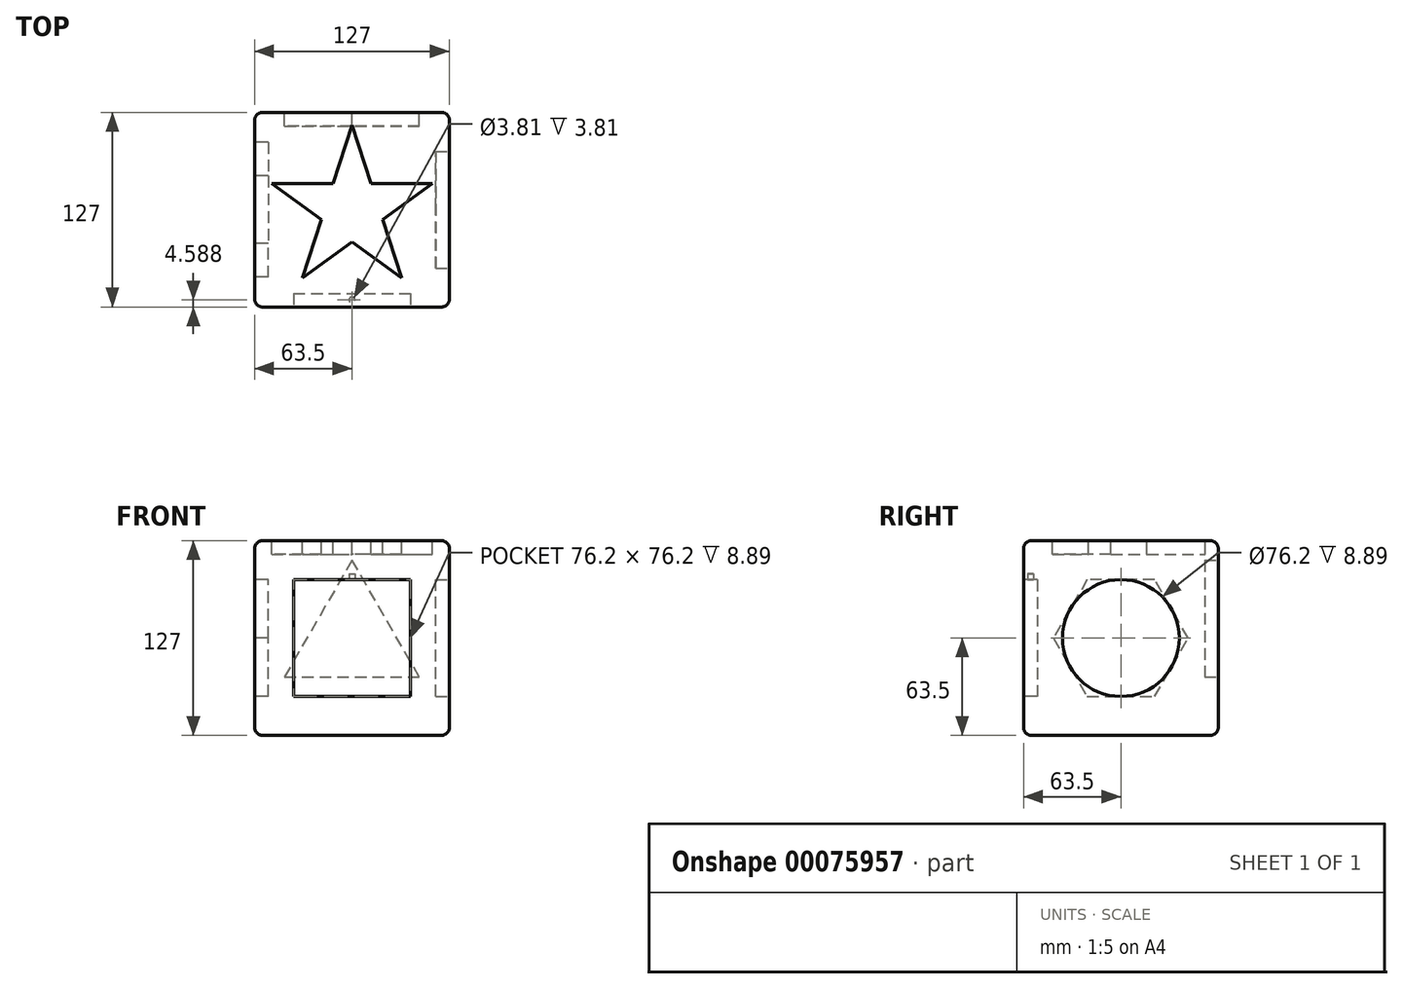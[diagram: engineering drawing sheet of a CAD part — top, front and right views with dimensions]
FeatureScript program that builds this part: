
annotation { "Feature Type Name" : "Feature", "Feature Type Description" : "" }
export const myFeature = defineFeature(function(context is Context, id is Id, definition is map)
    precondition{}
    {
        {
            var Q0;
            Q0=qCreatedBy(makeId("Top.planeOp"),FACE);
            var sketch = newSketch(context, id + "F0", { "sketchPlane" : qUnion([Q0])});
            skLineSegment(sketch, "E0.bottom", {"start": v(-63.5, 63.5) * mm, "end": v(63.5, 63.5) * mm});
            skLineSegment(sketch, "E0.top", {"start": v(-63.5, -63.5) * mm, "end": v(63.5, -63.5) * mm});
            skLineSegment(sketch, "E0.left", {"start": v(-63.5, 63.5) * mm, "end": v(-63.5, -63.5) * mm});
            skLineSegment(sketch, "E0.right", {"start": v(63.5, 63.5) * mm, "end": v(63.5, -63.5) * mm});
            skPoint(sketch, "E0.middle", {"position": v(0, 0) * mm});
            skSolve(sketch);
        }
        {
            var Q0;
            Q0=qSketchRegion(id+"F0",true);
            extrude(context, id + "F1", {"entities" : qUnion([Q0]), "oppositeDirection" : true, "depth" : 63.5 * mm});
        }
        {
            var Q0;
            Q0=makeQuery(id+"F1.opExtrude","CAP_FACE",FACE,{"disambiguationData":[OSD([sQuery(id+"F0.wireOp",EDGE,"E0.bottom"),sQuery(id+"F0.wireOp",EDGE,"E0.top"),sQuery(id+"F0.wireOp",EDGE,"E0.left"),sQuery(id+"F0.wireOp",EDGE,"E0.right")])],"isStart":true});
            extrude(context, id + "F2", {"entities" : qUnion([Q0]), "operationType" : NewBodyOperationType.ADD, "depth" : 63.5 * mm});
        }
        {
            var Q0;
            {var subQ0=sQuery(id+"F0.wireOp",EDGE,"E0.top");Q0=makeQuery(id+"F2.boolean.opBoolean","MERGE",FACE,{"derivedFrom":[makeQuery(id+"F1.opExtrude","SWEPT_FACE",FACE,{"disambiguationData":[OSD([subQ0])]}),makeQuery(id+"F2.opExtrude","SWEPT_FACE",FACE,{"disambiguationData":[OSD([subQ0])]})]});}
            var sketch = newSketch(context, id + "F3", { "sketchPlane" : qUnion([Q0])});
            skLineSegment(sketch, "E1.bottom", {"start": v(-38.1, 38.1) * mm, "end": v(38.1, 38.1) * mm});
            skLineSegment(sketch, "E1.top", {"start": v(-38.1, -38.1) * mm, "end": v(38.1, -38.1) * mm});
            skLineSegment(sketch, "E1.left", {"start": v(-38.1, 38.1) * mm, "end": v(-38.1, -38.1) * mm});
            skLineSegment(sketch, "E1.right", {"start": v(38.1, 38.1) * mm, "end": v(38.1, -38.1) * mm});
            skPoint(sketch, "E1.middle", {"position": v(0, 0) * mm});
            skSolve(sketch);
        }
        {
            var Q0;
            Q0=makeQuery(id+"F3.imprint","IMPRINT",FACE,{"disambiguationData":[TD([[makeQuery(id+"F3.imprint","IMPRINT",EDGE,{"derivedFrom":sQuery(id+"F3.wireOp",EDGE,"E1.bottom")}),-1.0]])]});
            extrude(context, id + "F4", {"entities" : qUnion([Q0]), "operationType" : NewBodyOperationType.REMOVE, "oppositeDirection" : true, "depth" : 8.9 * mm});
        }
        {
            var Q0;
            {var subQ0=sQuery(id+"F0.wireOp",EDGE,"E0.right");Q0=makeQuery(id+"F2.boolean.opBoolean","MERGE",FACE,{"derivedFrom":[makeQuery(id+"F1.opExtrude","SWEPT_FACE",FACE,{"disambiguationData":[OSD([subQ0])]}),makeQuery(id+"F2.opExtrude","SWEPT_FACE",FACE,{"disambiguationData":[OSD([subQ0])]})]});}
            var sketch = newSketch(context, id + "F5", { "sketchPlane" : qUnion([Q0])});
            skCircle(sketch, "E2", {"center": v(0, 0) * mm, "radius": 38.1 * mm});
            skSolve(sketch);
        }
        {
            var Q0;
            Q0=makeQuery(id+"F5.imprint","IMPRINT",FACE,{"disambiguationData":[TD([[makeQuery(id+"F5.imprint","IMPRINT",EDGE,{"derivedFrom":sQuery(id+"F5.wireOp",EDGE,"E2")}),1.0]])]});
            extrude(context, id + "F6", {"entities" : qUnion([Q0]), "operationType" : NewBodyOperationType.REMOVE, "oppositeDirection" : true, "depth" : 8.9 * mm});
        }
        {
            var Q0;
            {var subQ0=sQuery(id+"F0.wireOp",EDGE,"E0.bottom");Q0=makeQuery(id+"F2.boolean.opBoolean","MERGE",FACE,{"derivedFrom":[makeQuery(id+"F1.opExtrude","SWEPT_FACE",FACE,{"disambiguationData":[OSD([subQ0])]}),makeQuery(id+"F2.opExtrude","SWEPT_FACE",FACE,{"disambiguationData":[OSD([subQ0])]})]});}
            var sketch = newSketch(context, id + "F7", { "sketchPlane" : qUnion([Q0])});
            skCircle(sketch, "E3.cCircle", {"center": v(0, 0) * mm, "radius": 25.4 * mm, "construction": true});
            skLineSegment(sketch, "E3.0", {"start": v(44, -25.4) * mm, "end": v(-44, -25.4) * mm});
            skLineSegment(sketch, "E3.1", {"start": v(-44, -25.4) * mm, "end": v(0, 50.8) * mm});
            skLineSegment(sketch, "E3.2", {"start": v(0, 50.8) * mm, "end": v(44, -25.4) * mm});
            skPoint(sketch, "E3.0.midPoint", {"position": v(0, -25.4) * mm});
            skSolve(sketch);
        }
        {
            var Q0;
            Q0=makeQuery(id+"F7.imprint","IMPRINT",FACE,{"disambiguationData":[TD([[makeQuery(id+"F7.imprint","IMPRINT",EDGE,{"derivedFrom":sQuery(id+"F7.wireOp",EDGE,"E3.0")}),-1.0]])]});
            extrude(context, id + "F8", {"entities" : qUnion([Q0]), "operationType" : NewBodyOperationType.REMOVE, "oppositeDirection" : true, "depth" : 8.9 * mm});
        }
        {
            var Q0;
            {var subQ0=sQuery(id+"F0.wireOp",EDGE,"E0.left");Q0=makeQuery(id+"F2.boolean.opBoolean","MERGE",FACE,{"derivedFrom":[makeQuery(id+"F1.opExtrude","SWEPT_FACE",FACE,{"disambiguationData":[OSD([subQ0])]}),makeQuery(id+"F2.opExtrude","SWEPT_FACE",FACE,{"disambiguationData":[OSD([subQ0])]})]});}
            var sketch = newSketch(context, id + "F9", { "sketchPlane" : qUnion([Q0])});
            skCircle(sketch, "E4.cCircle", {"center": v(0, 0) * mm, "radius": 38.1 * mm, "construction": true});
            skLineSegment(sketch, "E4.0", {"start": v(-22, 38.1) * mm, "end": v(22, 38.1) * mm});
            skLineSegment(sketch, "E4.1", {"start": v(22, 38.1) * mm, "end": v(44, 0) * mm});
            skLineSegment(sketch, "E4.2", {"start": v(44, 0) * mm, "end": v(22, -38.1) * mm});
            skLineSegment(sketch, "E4.3", {"start": v(22, -38.1) * mm, "end": v(-22, -38.1) * mm});
            skLineSegment(sketch, "E4.4", {"start": v(-22, -38.1) * mm, "end": v(-44, 0) * mm});
            skLineSegment(sketch, "E4.5", {"start": v(-44, 0) * mm, "end": v(-22, 38.1) * mm});
            skPoint(sketch, "E4.0.midPoint", {"position": v(0, 38.1) * mm});
            skSolve(sketch);
        }
        {
            var Q0;
            Q0=makeQuery(id+"F9.imprint","IMPRINT",FACE,{"disambiguationData":[TD([[makeQuery(id+"F9.imprint","IMPRINT",EDGE,{"derivedFrom":sQuery(id+"F9.wireOp",EDGE,"E4.0")}),-1.0]])]});
            extrude(context, id + "F10", {"entities" : qUnion([Q0]), "operationType" : NewBodyOperationType.REMOVE, "oppositeDirection" : true, "depth" : 8.9 * mm});
        }
        {
            var Q0;
            Q0=makeQuery(id+"F2.opExtrude","CAP_FACE",FACE,{"disambiguationData":[OSD([sQuery(id+"F0.wireOp",EDGE,"E0.bottom"),sQuery(id+"F0.wireOp",EDGE,"E0.top"),sQuery(id+"F0.wireOp",EDGE,"E0.left"),sQuery(id+"F0.wireOp",EDGE,"E0.right")])],"isStart":false});
            var sketch = newSketch(context, id + "F11", { "sketchPlane" : qUnion([Q0])});
            skCircle(sketch, "E5.cCircle", {"center": v(0, 0) * mm, "radius": 17.04 * mm, "construction": true});
            skPoint(sketch, "E5.0.midPoint", {"position": v(0, 17.04) * mm});
            skLineSegment(sketch, "E6", {"start": v(-12.38, 17.04) * mm, "end": v(0, 55.14) * mm});
            skLineSegment(sketch, "E7", {"start": v(12.38, 17.04) * mm, "end": v(0, 55.14) * mm});
            skLineSegment(sketch, "E8", {"start": v(12.38, 17.04) * mm, "end": v(52.44, 17.04) * mm});
            skLineSegment(sketch, "E9", {"start": v(20.03, -6.5) * mm, "end": v(52.44, 17.04) * mm});
            skLineSegment(sketch, "E10", {"start": v(20.03, -6.5) * mm, "end": v(32.4, -44.6) * mm});
            skLineSegment(sketch, "E11", {"start": v(32.4, -44.6) * mm, "end": v(0, -21.06) * mm});
            skLineSegment(sketch, "E12", {"start": v(-32.4, -44.6) * mm, "end": v(0, -21.06) * mm});
            skLineSegment(sketch, "E13", {"start": v(-20.03, -6.5) * mm, "end": v(-32.4, -44.6) * mm});
            skLineSegment(sketch, "E14", {"start": v(-20.03, -6.5) * mm, "end": v(-52.44, 17.04) * mm});
            skLineSegment(sketch, "E15", {"start": v(-52.44, 17.04) * mm, "end": v(-12.38, 17.04) * mm});
            skSolve(sketch);
        }
        {
            var Q0;
            Q0=makeQuery(id+"F11.imprint","IMPRINT",FACE,{"disambiguationData":[TD([[makeQuery(id+"F11.imprint","IMPRINT",EDGE,{"derivedFrom":sQuery(id+"F11.wireOp",EDGE,"E6")}),-1.0]])]});
            extrude(context, id + "F12", {"entities" : qUnion([Q0]), "operationType" : NewBodyOperationType.REMOVE, "oppositeDirection" : true, "depth" : 8.9 * mm});
        }
        {
            var Q0;
            Q0=makeQuery(id+"F2.opExtrude","CAP_EDGE",EDGE,{"disambiguationData":[OSD([sQuery(id+"F0.wireOp",EDGE,"E0.left")])],"isStart":false});
            var Q1;
            Q1=makeQuery(id+"F2.opExtrude","CAP_EDGE",EDGE,{"disambiguationData":[OSD([sQuery(id+"F0.wireOp",EDGE,"E0.bottom")])],"isStart":false});
            var Q2;
            Q2=makeQuery(id+"F2.opExtrude","CAP_EDGE",EDGE,{"disambiguationData":[OSD([sQuery(id+"F0.wireOp",EDGE,"E0.right")])],"isStart":false});
            var Q3;
            Q3=makeQuery(id+"F2.opExtrude","CAP_EDGE",EDGE,{"disambiguationData":[OSD([sQuery(id+"F0.wireOp",EDGE,"E0.top")])],"isStart":false});
            var Q4;
            {var subQ0=sQuery(id+"F0.wireOp",EDGE,"E0.right");var subQ1=sQuery(id+"F0.wireOp",EDGE,"E0.top");Q4=makeQuery(id+"F2.boolean.opBoolean","MERGE",EDGE,{"derivedFrom":[makeQuery(id+"F1.opExtrude","SWEPT_EDGE",EDGE,{"disambiguationData":[OSD([subQ1,subQ0])]}),makeQuery(id+"F2.opExtrude","SWEPT_EDGE",EDGE,{"disambiguationData":[OSD([subQ1,subQ0])]})]});}
            var Q5;
            {var subQ0=sQuery(id+"F0.wireOp",EDGE,"E0.right");var subQ1=sQuery(id+"F0.wireOp",EDGE,"E0.bottom");Q5=makeQuery(id+"F2.boolean.opBoolean","MERGE",EDGE,{"derivedFrom":[makeQuery(id+"F1.opExtrude","SWEPT_EDGE",EDGE,{"disambiguationData":[OSD([subQ1,subQ0])]}),makeQuery(id+"F2.opExtrude","SWEPT_EDGE",EDGE,{"disambiguationData":[OSD([subQ1,subQ0])]})]});}
            var Q6;
            Q6=makeQuery(id+"F1.opExtrude","CAP_EDGE",EDGE,{"disambiguationData":[OSD([sQuery(id+"F0.wireOp",EDGE,"E0.right")])],"isStart":false});
            var Q7;
            Q7=makeQuery(id+"F1.opExtrude","CAP_EDGE",EDGE,{"disambiguationData":[OSD([sQuery(id+"F0.wireOp",EDGE,"E0.top")])],"isStart":false});
            var Q8;
            {var subQ0=sQuery(id+"F0.wireOp",EDGE,"E0.left");var subQ1=sQuery(id+"F0.wireOp",EDGE,"E0.top");Q8=makeQuery(id+"F2.boolean.opBoolean","MERGE",EDGE,{"derivedFrom":[makeQuery(id+"F1.opExtrude","SWEPT_EDGE",EDGE,{"disambiguationData":[OSD([subQ1,subQ0])]}),makeQuery(id+"F2.opExtrude","SWEPT_EDGE",EDGE,{"disambiguationData":[OSD([subQ1,subQ0])]})]});}
            var Q9;
            Q9=makeQuery(id+"F1.opExtrude","CAP_EDGE",EDGE,{"disambiguationData":[OSD([sQuery(id+"F0.wireOp",EDGE,"E0.bottom")])],"isStart":false});
            var Q10;
            {var subQ0=sQuery(id+"F0.wireOp",EDGE,"E0.left");var subQ1=sQuery(id+"F0.wireOp",EDGE,"E0.bottom");Q10=makeQuery(id+"F2.boolean.opBoolean","MERGE",EDGE,{"derivedFrom":[makeQuery(id+"F1.opExtrude","SWEPT_EDGE",EDGE,{"disambiguationData":[OSD([subQ1,subQ0])]}),makeQuery(id+"F2.opExtrude","SWEPT_EDGE",EDGE,{"disambiguationData":[OSD([subQ1,subQ0])]})]});}
            var Q11;
            Q11=makeQuery(id+"F1.opExtrude","CAP_EDGE",EDGE,{"disambiguationData":[OSD([sQuery(id+"F0.wireOp",EDGE,"E0.left")])],"isStart":false});
            fillet(context, id + "F13", {"entities" : qUnion([Q0, Q1, Q2, Q3, Q4, Q5, Q6, Q7, Q8, Q9, Q10, Q11]), "radius" : 5.08 * mm, "tangentPropagation" : true, "allowEdgeOverflow" : false});
        }
        {
            var Q0;
            Q0=makeQuery(id+"F4.boolean.opBoolean","COPY",FACE,{"derivedFrom":makeQuery(id+"F4.opExtrude","SWEPT_FACE",FACE,{"disambiguationData":[OSD([sQuery(id+"F3.wireOp",EDGE,"E1.bottom")])]})});
            var sketch = newSketch(context, id + "F14", { "sketchPlane" : qUnion([Q0])});
            skCircle(sketch, "E16", {"center": v(0, 58.91) * mm, "radius": 1.9 * mm});
            skPoint(sketch, "E17", {"position": v(0, 63.5) * mm});
            skSolve(sketch);
        }
        {
            var Q0;
            Q0 = qSketchRegion(id + "F14", true);
            extrude(context, id + "F15", {"entities" : qUnion([Q0]), "operationType" : NewBodyOperationType.REMOVE, "oppositeDirection" : true, "depth" : 3.8 * mm});
        }
    });
